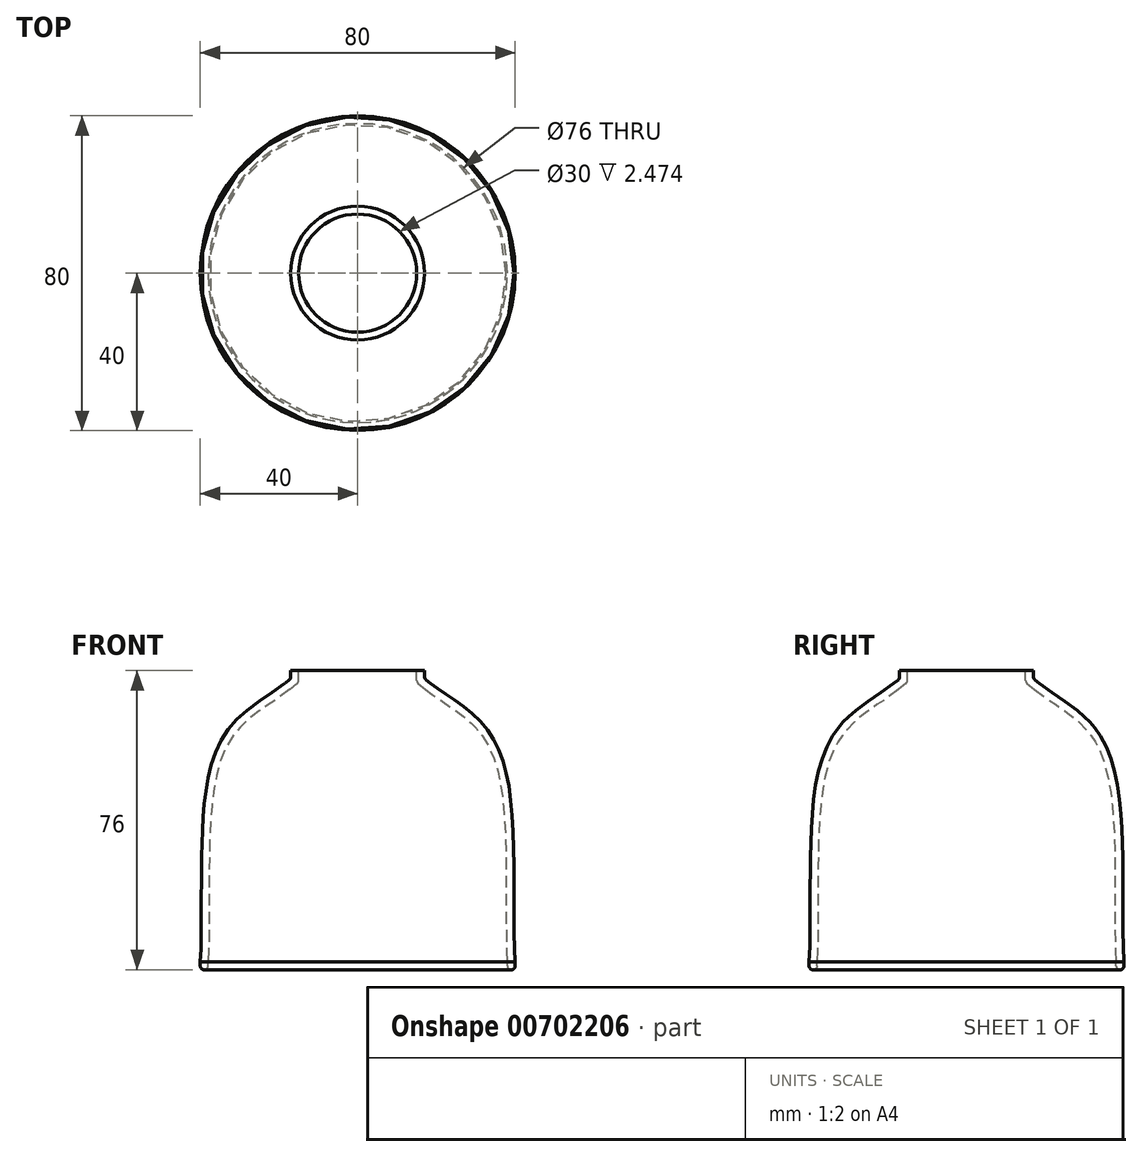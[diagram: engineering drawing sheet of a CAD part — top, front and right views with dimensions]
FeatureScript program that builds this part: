
annotation { "Feature Type Name" : "Feature", "Feature Type Description" : "" }
export const myFeature = defineFeature(function(context is Context, id is Id, definition is map)
    precondition{}
    {
        {
            var Q0;
            Q0=qCreatedBy(makeId("Front.planeOp"),FACE);
            var sketch = newSketch(context, id + "F0", { "sketchPlane" : qUnion([Q0])});
            skLineSegment(sketch, "E0", {"start": v(-17, 18.55) * mm, "end": v(-17, 16.55) * mm});
            skLineSegment(sketch, "E1", {"start": v(-17, 16.55) * mm, "end": v(-18.55, 15.28) * mm});
            skFitSpline(sketch, "E2", {"points": [v(-18.55, 15.28) * mm, v(-31.43, 5.4) * mm, v(-39.05, -15.92) * mm, v(-40, -55.45) * mm], "startDerivative": vector(-35.75, -29.27) * mm, "endDerivative": vector(-4.6, -76.55) * mm});
            skLineSegment(sketch, "E3", {"start": v(-40, -55.45) * mm, "end": v(-40, -57.45) * mm});
            skLineSegment(sketch, "E4.0", {"start": v(-38, -55.51) * mm, "end": v(-38, -57.45) * mm});
            skFitSpline(sketch, "E4.1", {"points": [v(-17.28, 13.73) * mm, v(-18.1, 13.06) * mm, v(-19.96, 11.74) * mm, v(-23.12, 9.66) * mm, v(-25.81, 7.76) * mm, v(-27.84, 6.11) * mm, v(-29.02, 5.02) * mm, v(-29.9, 4.12) * mm, v(-30.7, 3.2) * mm, v(-32.03, 1.48) * mm, v(-33.6, -1.24) * mm, v(-35.07, -5.02) * mm, v(-35.98, -8.63) * mm, v(-36.54, -11.81) * mm, v(-36.88, -14.35) * mm, v(-37.15, -17.04) * mm, v(-37.43, -20.82) * mm, v(-37.63, -25.85) * mm, v(-37.73, -32.13) * mm, v(-37.73, -38.46) * mm, v(-37.73, -44.63) * mm, v(-37.78, -50.44) * mm, v(-37.9, -53.94) * mm, v(-38, -55.57) * mm]});
            skLineSegment(sketch, "E4.2", {"start": v(-15, 15.6) * mm, "end": v(-17.28, 13.73) * mm});
            skLineSegment(sketch, "E4.3", {"start": v(-15, 18.55) * mm, "end": v(-15, 15.6) * mm});
            skLineSegment(sketch, "E5", {"start": v(-40, -57.45) * mm, "end": v(-38, -57.45) * mm});
            skLineSegment(sketch, "E6", {"start": v(-17, 18.55) * mm, "end": v(-15, 18.55) * mm});
            skLineSegment(sketch, "E7", {"start": v(0, 24.17) * mm, "end": v(0, -71.74) * mm, "construction": true});
            skSolve(sketch);
        }
        {
            var Q0;
            Q0 = qSketchRegion(id + "F0", true);
            var Q1;
            Q1=sQuery(id+"F0.wireOp",EDGE,"E7");
            revolve(context, id + "F1", {"entities" : qUnion([Q0]), "axis" : qUnion([Q1]), "revolveType" : RevolveType.FULL});
        }
        {
            var Q0;
            Q0=makeQuery(id+"F1.opRevolve","SWEPT_FACE",FACE,{"disambiguationData":[OSD([sQuery(id+"F0.wireOp",EDGE,"E5")])]});
            var Q1;
            Q1=makeQuery(id+"F1.opRevolve","SWEPT_EDGE",EDGE,{"disambiguationData":[OSD([sQuery(id+"F0.wireOp",EDGE,"E0"),sQuery(id+"F0.wireOp",EDGE,"E1")])]});
            var Q2;
            Q2=makeQuery(id+"F1.opRevolve","SWEPT_EDGE",EDGE,{"disambiguationData":[OSD([sQuery(id+"F0.wireOp",EDGE,"E4.2"),sQuery(id+"F0.wireOp",EDGE,"E4.3")])]});
            var Q3;
            Q3=makeQuery(id+"F1.opRevolve","SWEPT_EDGE",EDGE,{"disambiguationData":[OSD([sQuery(id+"F0.wireOp",EDGE,"E4.1"),sQuery(id+"F0.wireOp",EDGE,"E4.2")])]});
            fillet(context, id + "F2", {"entities" : qUnion([Q0, Q1, Q2, Q3]), "radius" : 1 * mm, "tangentPropagation" : true, "allowEdgeOverflow" : false});
        }
    });
